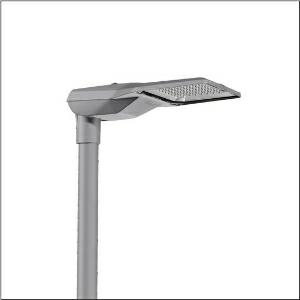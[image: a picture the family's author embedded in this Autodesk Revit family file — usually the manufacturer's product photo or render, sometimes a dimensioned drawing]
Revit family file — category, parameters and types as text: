
# Revit family: streetlight_sl_21_midi___st1_0a_5xe3d43s08nb_04c9
name_source: partatom
category: Lighting Fixtures
units: mm (PartAtom-declared; Revit-internal decimal feet)

## family parameters
Cut with Voids When Loaded = No
Host = Face
Light Source = No
Part Type = Normal
Room Calculation Point = No
Round Connector Dimension = Use Diameter
Shared = No

## types (1)
- --- (1 x LED, 23710 lm, 151.2 W, 4000K)
    Apparent Load = 151 VA
    CIE Flux Codes = 40 73 97 100 100
    Color Rendering = 70
    Color Temperature = 4000K
    Default Elevation = 1800 mm
    Description = Streetlight SL 21 midi, mast luminaire, primary light control with lens, of PMMA, primary optical cover: cover, of toughened safety glass, transparent, light distribution: ST1.0a, light emission: direct distribution, primary light characteristic: asymmetric, installation type: side-entry, post-top, LED, High Power LED, rated luminous flux: 23.710lm, luminous efficacy: 157lm/W, light colour: 740, colour temperature: 4000K, control gear: D4i, control: overheat protection, constant luminous flux control, time-dependent luminous flux control, flexible luminous flux parameterisation, pre-setting: logarithmic dimming characteristic, mains connection: 230..240V, AC, 50/60Hz, start of lifetime: 151W, end of service life: 157W, reduction: 70W, luminaire housing, of diecast aluminium, powder-coated, SITECO metallic grey (DB 702S), corrosivity category C5 high according to DIN EN ISO 12944, please order mast flange separately, inclination adjustable: 0°, 5°, 10°, 15°, sealing non-destructively replaceable, multi-level sealing system, length: 644mm, width: 335mm, height: 110mm, mast flange for spigot size: 42mm (side-entry): 5XC10008XM4, 60/48mm (side-entry/post-top): 5XC10108XM2, 76/60mm (side-entry/post-top): 5XC10108XM1, mounting height: 4..8m, Smart Interface above, protection rating (complete): IP66, insulation class (complete): insulation class II (safety insulation), certification: CE, ENEC, ENEC+, VDE, impact resistance: IK10, permissible operating ambient temperature for outdoor applications: -40..+50°C, standard-compliant lighting for roads and squares, packaging unit: 1 piece

Light Distribution: ST1.0a
    Height = 111 mm
    Lamp = 1 x LED
    Lamp Light Flux = 23710 lm
    Lamp Power = 151.2 W
    Lamp count = 1
    Length = 644 mm
    Luminous efficacy = 157 lm/W
    Manufacturer = Siteco
    ModVariant = No
    Model = 5XE3D43S08NB
    Number of Poles = 1
    OnlyDefault = Yes
    Power Factor = 1
    Product Name = Streetlight SL 21 midi | ST1.0a
    Product group = mast luminaire | pylon top
    ProductGroupID = 6100
    Protection Class = Protection class II
    Protection Degree = IP 66
    RLX_Detail_Level = 1
    RLX_Emergency_Light_Flux = 0 lm
    RLX_Emergency_Type = 0
    RLX_Emergency_Type_DB = No
    RlxData = <blob elided: 27009 chars, md5=f1df4ed0>
    Socket = socket
    Standby Power = 0 W
    System Light Flux = 23710 lm
    System Power = 151 W
    Type Comments = factory setting: luminous flux: 100 % | dim-lin: 254 | 802 mA
    Type Image = l_1004302.jpg
    URL = http://relux.com
    VarID = @adj_170053
    Voltage = 0 V
    Weight = 0.00 kg
    Width = 336 mm

## geometry (parser evidence)
native form markers: Blend x4, Sweep x10
no freeform markers — native parametric forms only
